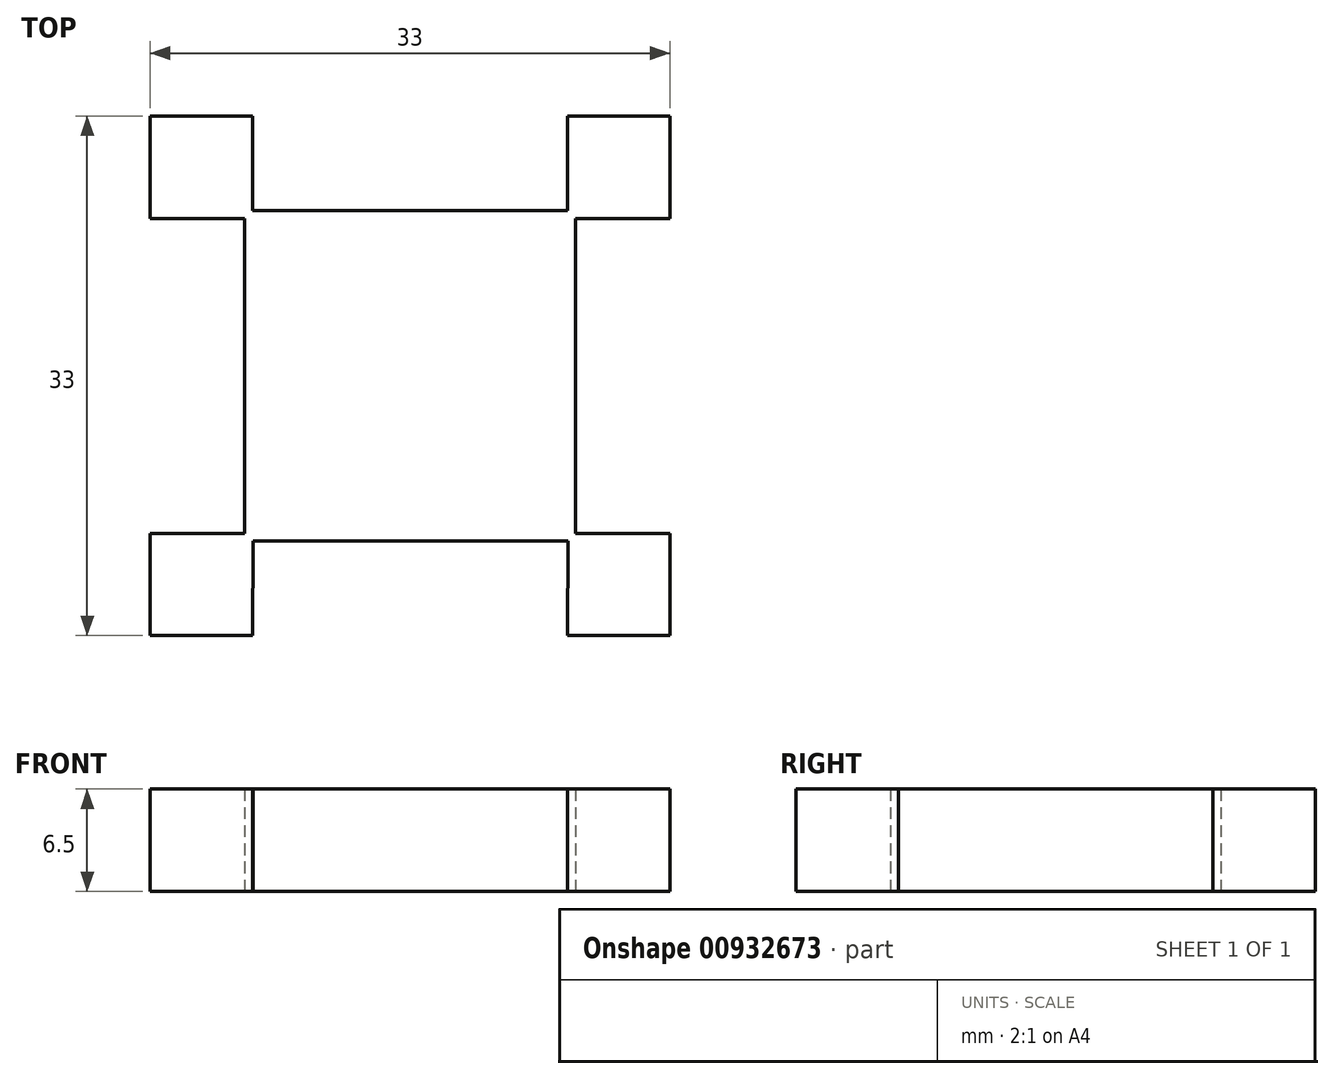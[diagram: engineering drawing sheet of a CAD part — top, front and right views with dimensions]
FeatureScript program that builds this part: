
annotation { "Feature Type Name" : "Feature", "Feature Type Description" : "" }
export const myFeature = defineFeature(function(context is Context, id is Id, definition is map)
    precondition{}
    {
        {
            var Q0;
            Q0=qCreatedBy(makeId("Top.planeOp"),FACE);
            var sketch = newSketch(context, id + "F0", { "sketchPlane" : qUnion([Q0])});
            skLineSegment(sketch, "E0.bottom", {"start": v(-16.5, 16.5) * mm, "end": v(-10, 16.5) * mm});
            skLineSegment(sketch, "E0.top", {"start": v(-16.5, -16.5) * mm, "end": v(-10, -16.5) * mm});
            skLineSegment(sketch, "E0.left", {"start": v(-16.5, 16.5) * mm, "end": v(-16.5, 10) * mm});
            skLineSegment(sketch, "E0.right", {"start": v(16.5, 16.5) * mm, "end": v(16.5, 10) * mm});
            skPoint(sketch, "E0.middle", {"position": v(0, 0) * mm});
            skLineSegment(sketch, "E1.bottom", {"start": v(16.5, -10) * mm, "end": v(10.5, -10) * mm});
            skLineSegment(sketch, "E1.top", {"start": v(16.5, 10) * mm, "end": v(10.5, 10) * mm});
            skLineSegment(sketch, "E1.right", {"start": v(10.5, -10) * mm, "end": v(10.5, 10) * mm});
            skLineSegment(sketch, "E2.top", {"start": v(-10, 10.5) * mm, "end": v(10, 10.5) * mm});
            skLineSegment(sketch, "E2.left", {"start": v(-10, 16.5) * mm, "end": v(-10, 10.5) * mm});
            skLineSegment(sketch, "E2.right", {"start": v(10, 16.5) * mm, "end": v(10, 10.5) * mm});
            skLineSegment(sketch, "E3.bottom", {"start": v(-10.5, 10) * mm, "end": v(-16.5, 10) * mm});
            skLineSegment(sketch, "E3.top", {"start": v(-10.5, -10) * mm, "end": v(-16.5, -10) * mm});
            skLineSegment(sketch, "E3.left", {"start": v(-10.5, 10) * mm, "end": v(-10.5, -10) * mm});
            skLineSegment(sketch, "E4.bottom", {"start": v(-9.97, -10.5) * mm, "end": v(10.03, -10.5) * mm});
            skLineSegment(sketch, "E4.left", {"start": v(-9.97, -10.5) * mm, "end": v(-10, -16.5) * mm});
            skLineSegment(sketch, "E4.right", {"start": v(10.03, -10.5) * mm, "end": v(10, -16.5) * mm});
            skLineSegment(sketch, "E5.trimOffspring", {"start": v(10, 16.5) * mm, "end": v(16.5, 16.5) * mm});
            skLineSegment(sketch, "E6.trimOffspring", {"start": v(-16.5, -10) * mm, "end": v(-16.5, -16.5) * mm});
            skLineSegment(sketch, "E7.trimOffspring", {"start": v(10, -16.5) * mm, "end": v(16.5, -16.5) * mm});
            skLineSegment(sketch, "E8.trimOffspring", {"start": v(16.5, -10) * mm, "end": v(16.5, -16.5) * mm});
            skSolve(sketch);
        }
        {
            var Q0;
            Q0=makeQuery(id+"F0.imprint","IMPRINT",FACE,{"disambiguationData":[TD([[makeQuery(id+"F0.imprint","IMPRINT",EDGE,{"derivedFrom":sQuery(id+"F0.wireOp",EDGE,"E0.bottom")}),-1.0]])]});
            var Q1;
            Q1=makeQuery(id+"F0.imprint","IMPRINT",FACE,{"disambiguationData":[TD([[makeQuery(id+"F0.imprint","IMPRINT",EDGE,{"derivedFrom":sQuery(id+"F0.wireOp",EDGE,"E0.top")}),1.0]])]});
            var Q2;
            Q2=makeQuery(id+"F0.imprint","IMPRINT",FACE,{"disambiguationData":[TD([[makeQuery(id+"F0.imprint","IMPRINT",EDGE,{"derivedFrom":sQuery(id+"F0.wireOp",EDGE,"E0.right")}),-1.0]])]});
            var Q3;
            Q3=makeQuery(id+"F0.imprint","IMPRINT",FACE,{"disambiguationData":[TD([[makeQuery(id+"F0.imprint","IMPRINT",EDGE,{"derivedFrom":sQuery(id+"F0.wireOp",EDGE,"E1.bottom")}),1.0]])]});
            extrude(context, id + "F1", {"entities" : qUnion([Q0, Q1, Q2, Q3]), "depth" : 6.5 * mm, "offsetDistance" : 25 * mm});
        }
    });
